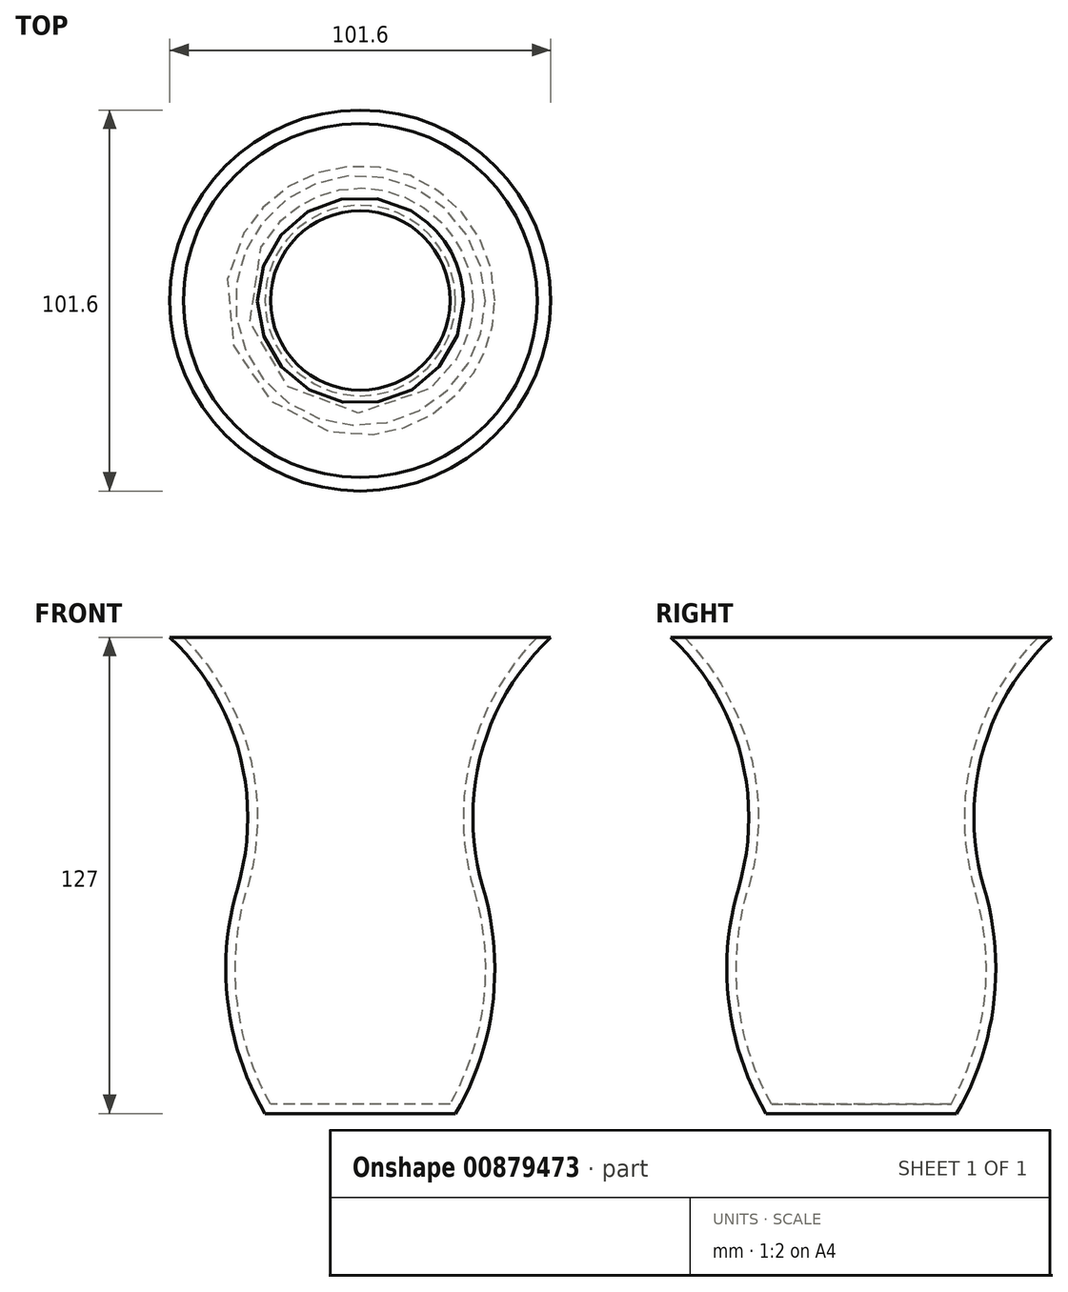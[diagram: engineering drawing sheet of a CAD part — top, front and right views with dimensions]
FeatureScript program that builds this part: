
annotation { "Feature Type Name" : "Feature", "Feature Type Description" : "" }
export const myFeature = defineFeature(function(context is Context, id is Id, definition is map)
    precondition{}
    {
        {
            var Q0;
            Q0=qCreatedBy(makeId("Front.planeOp"),FACE);
            var sketch = newSketch(context, id + "F0", { "sketchPlane" : qUnion([Q0])});
            skLineSegment(sketch, "E0", {"start": v(0, -60.2) * mm, "end": v(-25.4, -60.2) * mm});
            skArc(sketch, "E1", {"start": v(-32.73, 0) * mm, "mid": v(-35.31, -30.86) * mm, "end": v(-25.4, -60.2) * mm});
            skArc(sketch, "E2", {"start": v(-32.73, 0) * mm, "mid": v(-32.3, 35.96) * mm, "end": v(-50.8, 66.8) * mm});
            skLineSegment(sketch, "E3", {"start": v(-50.8, 66.8) * mm, "end": v(0, 66.8) * mm});
            skLineSegment(sketch, "E4", {"start": v(0, 66.8) * mm, "end": v(0, -60.2) * mm});
            skSolve(sketch);
        }
        {
            var Q0;
            Q0=makeQuery(id+"F0.imprint","IMPRINT",FACE,{"disambiguationData":[TD([[makeQuery(id+"F0.imprint","IMPRINT",EDGE,{"derivedFrom":sQuery(id+"F0.wireOp",EDGE,"E0")}),-1.0]])]});
            var Q1;
            Q1=sQuery(id+"F0.wireOp",EDGE,"E4");
            revolve(context, id + "F1", {"surfaceOperationType" : NewSurfaceOperationType.NEW, "entities" : qUnion([Q0]), "axis" : qUnion([Q1]), "revolveType" : RevolveType.FULL});
        }
        {
            var Q0;
            Q0=makeQuery(id+"F1.opRevolve","SWEPT_FACE",FACE,{"disambiguationData":[OSD([sQuery(id+"F0.wireOp",EDGE,"E3")])]});
            shell(context, id + "F2", {"entities" : qUnion([Q0]), "thickness" : 2.54 * mm});
        }
    });
